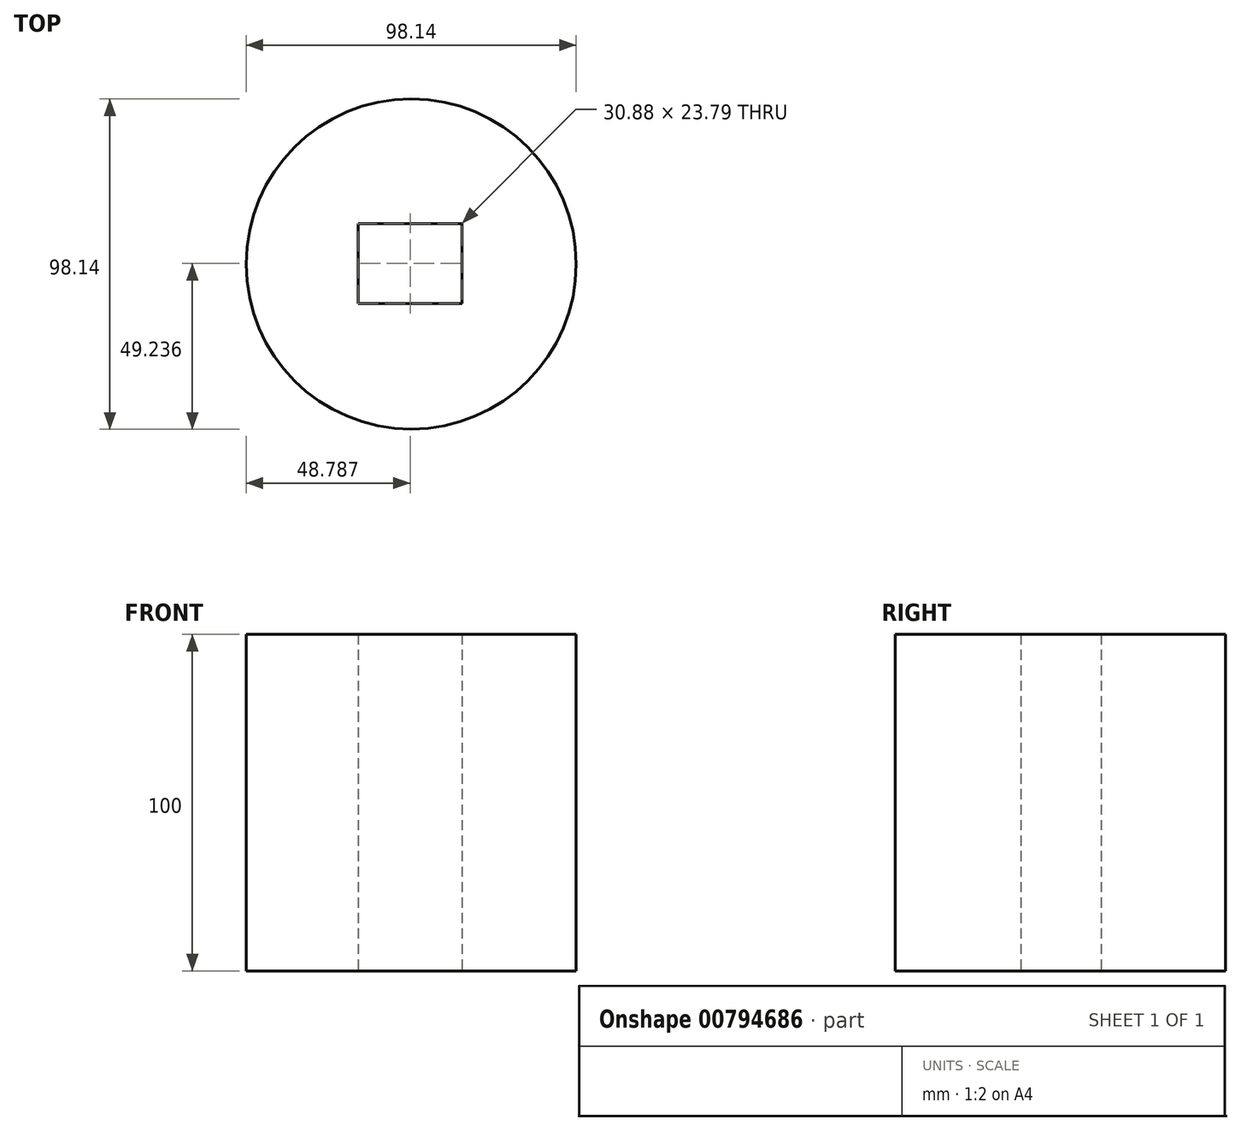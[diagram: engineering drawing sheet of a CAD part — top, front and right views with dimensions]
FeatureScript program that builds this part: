
annotation { "Feature Type Name" : "Feature", "Feature Type Description" : "" }
export const myFeature = defineFeature(function(context is Context, id is Id, definition is map)
    precondition{}
    {
        {
            var Q0;
            Q0=qCreatedBy(makeId("Top.planeOp"),FACE);
            var sketch = newSketch(context, id + "F0", { "sketchPlane" : qUnion([Q0])});
            skCircle(sketch, "E0", {"center": v(0, 0) * mm, "radius": 49.07 * mm});
            skSolve(sketch);
        }
        {
            var Q0;
            Q0 = qSketchRegion(id + "F0", true);
            extrude(context, id + "F1", {"entities" : qUnion([Q0]), "depth" : 100 * mm, "offsetDistance" : 25 * mm});
        }
        {
            var Q0;
            Q0=makeQuery(id+"F1.opExtrude","CAP_FACE",FACE,{"disambiguationData":[OSD([sQuery(id+"F0.wireOp",EDGE,"E0")])],"isStart":true});
            var sketch = newSketch(context, id + "F2", { "sketchPlane" : qUnion([Q0])});
            skLineSegment(sketch, "E1.bottom", {"start": v(-15.72, 11.73) * mm, "end": v(15.16, 11.73) * mm});
            skLineSegment(sketch, "E1.top", {"start": v(-15.72, -12.06) * mm, "end": v(15.16, -12.06) * mm});
            skLineSegment(sketch, "E1.left", {"start": v(-15.72, 11.73) * mm, "end": v(-15.72, -12.06) * mm});
            skLineSegment(sketch, "E1.right", {"start": v(15.16, 11.73) * mm, "end": v(15.16, -12.06) * mm});
            skSolve(sketch);
        }
        {
            var Q0;
            Q0 = qSketchRegion(id + "F2", true);
            extrude(context, id + "F3", {"entities" : qUnion([Q0]), "operationType" : NewBodyOperationType.REMOVE, "oppositeDirection" : true, "depth" : 100 * mm, "offsetDistance" : 25 * mm});
        }
    });
